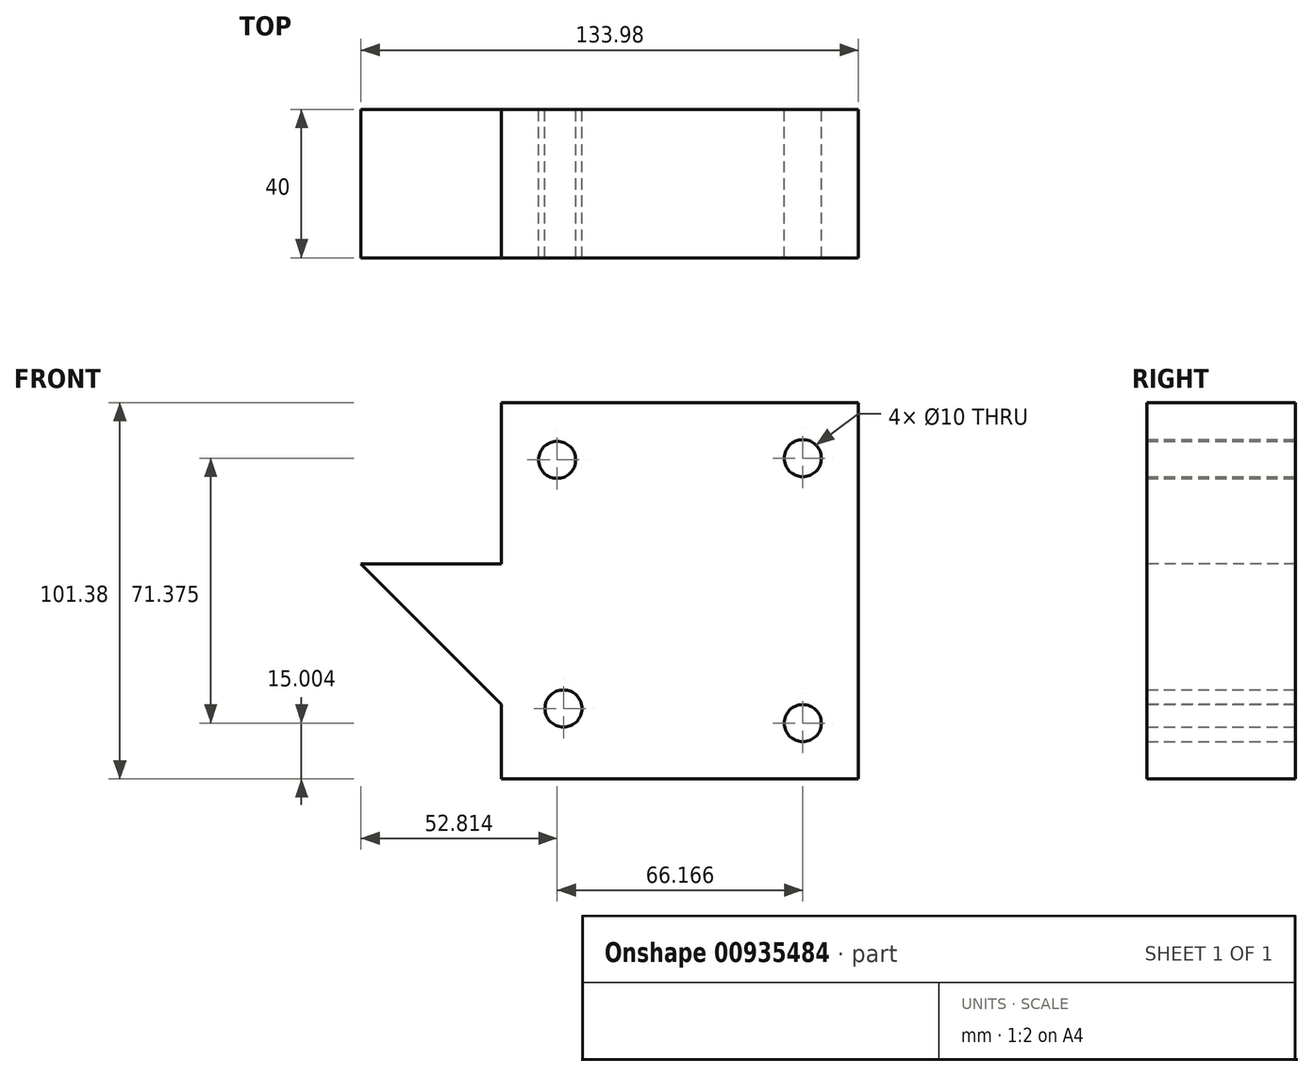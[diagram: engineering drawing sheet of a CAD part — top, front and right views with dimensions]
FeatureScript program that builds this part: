
annotation { "Feature Type Name" : "Feature", "Feature Type Description" : "" }
export const myFeature = defineFeature(function(context is Context, id is Id, definition is map)
    precondition{}
    {
        {
            var Q0;
            Q0=qCreatedBy(makeId("Front.planeOp"),FACE);
            var sketch = newSketch(context, id + "F0", { "sketchPlane" : qUnion([Q0])});
            skLineSegment(sketch, "E0", {"start": v(-1231.13, 861.68) * mm, "end": v(1231.13, 861.68) * mm});
            skLineSegment(sketch, "E1", {"start": v(1231.13, 861.68) * mm, "end": v(1231.13, -874.17) * mm});
            skLineSegment(sketch, "E2", {"start": v(1231.13, -874.17) * mm, "end": v(-1231.13, -874.17) * mm});
            skLineSegment(sketch, "E3", {"start": v(-1231.13, -874.17) * mm, "end": v(-1231.13, 861.68) * mm});
            skLineSegment(sketch, "E4", {"start": v(-731.13, 861.68) * mm, "end": v(-731.13, -874.17) * mm});
            skLineSegment(sketch, "E5.bottom", {"start": v(-55.5, 55.06) * mm, "end": v(40.67, 55.06) * mm});
            skLineSegment(sketch, "E5.top", {"start": v(-55.5, -46.32) * mm, "end": v(40.67, -46.32) * mm});
            skLineSegment(sketch, "E5.left", {"start": v(-55.5, 55.06) * mm, "end": v(-55.5, -46.32) * mm});
            skLineSegment(sketch, "E5.right", {"start": v(40.67, 55.06) * mm, "end": v(40.67, -46.32) * mm});
            skSolve(sketch);
        }
        {
            var Q0;
            Q0=makeQuery(id+"F0.imprint","IMPRINT",FACE,{"disambiguationData":[TD([[makeQuery(id+"F0.imprint","IMPRINT",EDGE,{"derivedFrom":sQuery(id+"F0.wireOp",EDGE,"E5.bottom")}),-1.0]])]});
            extrude(context, id + "F1", {"entities" : qUnion([Q0]), "depth" : 40 * mm, "offsetDistance" : 25 * mm});
        }
        {
            var Q0;
            Q0=makeQuery(id+"F1.opExtrude","CAP_FACE",FACE,{"disambiguationData":[OSD([sQuery(id+"F0.wireOp",EDGE,"E5.bottom"),sQuery(id+"F0.wireOp",EDGE,"E5.top"),sQuery(id+"F0.wireOp",EDGE,"E5.left"),sQuery(id+"F0.wireOp",EDGE,"E5.right")])],"isStart":false});
            var sketch = newSketch(context, id + "F2", { "sketchPlane" : qUnion([Q0])});
            skLineSegment(sketch, "E6", {"start": v(-55.5, -26.28) * mm, "end": v(-93.3, 11.53) * mm});
            skLineSegment(sketch, "E7", {"start": v(-93.3, 11.53) * mm, "end": v(-55.5, 11.53) * mm});
            skLineSegment(sketch, "E8", {"start": v(-55.5, 11.53) * mm, "end": v(-55.5, -26.28) * mm});
            skSolve(sketch);
        }
        {
            var Q0;
            Q0=makeQuery(id+"F2.imprint","IMPRINT",FACE,{"disambiguationData":[TD([[makeQuery(id+"F2.imprint","IMPRINT",EDGE,{"derivedFrom":sQuery(id+"F2.wireOp",EDGE,"E6")}),-1.0]])]});
            extrude(context, id + "F3", {"entities" : qUnion([Q0]), "operationType" : NewBodyOperationType.ADD, "oppositeDirection" : true, "depth" : 40 * mm, "offsetDistance" : 25 * mm});
        }
        {
            var Q0;
            Q0=makeQuery(id+"F3.boolean.opBoolean","MERGE",FACE,{"derivedFrom":[makeQuery(id+"F1.opExtrude","CAP_FACE",FACE,{"disambiguationData":[OSD([sQuery(id+"F0.wireOp",EDGE,"E5.bottom"),sQuery(id+"F0.wireOp",EDGE,"E5.top"),sQuery(id+"F0.wireOp",EDGE,"E5.left"),sQuery(id+"F0.wireOp",EDGE,"E5.right")])],"isStart":true}),makeQuery(id+"F3.opExtrude","CAP_FACE",FACE,{"disambiguationData":[OSD([sQuery(id+"F2.wireOp",EDGE,"E6"),sQuery(id+"F2.wireOp",EDGE,"E7"),sQuery(id+"F2.wireOp",EDGE,"E8")])],"isStart":false})]});
            var sketch = newSketch(context, id + "F4", { "sketchPlane" : qUnion([Q0])});
            skCircle(sketch, "E9", {"center": v(-25.67, -31.32) * mm, "radius": 5 * mm});
            skCircle(sketch, "E10", {"center": v(-25.67, 40.06) * mm, "radius": 5 * mm});
            skCircle(sketch, "E11", {"center": v(40.5, 39.62) * mm, "radius": 5 * mm});
            skCircle(sketch, "E12", {"center": v(38.79, -27.37) * mm, "radius": 5 * mm});
            skSolve(sketch);
        }
        {
            var Q0;
            Q0=makeQuery(id+"F4.imprint","IMPRINT",FACE,{"disambiguationData":[TD([[makeQuery(id+"F4.imprint","IMPRINT",EDGE,{"derivedFrom":sQuery(id+"F4.wireOp",EDGE,"E12")}),1.0]])]});
            var Q1;
            Q1=makeQuery(id+"F4.imprint","IMPRINT",FACE,{"disambiguationData":[TD([[makeQuery(id+"F4.imprint","IMPRINT",EDGE,{"derivedFrom":sQuery(id+"F4.wireOp",EDGE,"E9")}),1.0]])]});
            var Q2;
            Q2=makeQuery(id+"F4.imprint","IMPRINT",FACE,{"disambiguationData":[TD([[makeQuery(id+"F4.imprint","IMPRINT",EDGE,{"derivedFrom":sQuery(id+"F4.wireOp",EDGE,"E10")}),1.0]])]});
            var Q3;
            Q3=makeQuery(id+"F4.imprint","IMPRINT",FACE,{"disambiguationData":[TD([[makeQuery(id+"F4.imprint","IMPRINT",EDGE,{"derivedFrom":sQuery(id+"F4.wireOp",EDGE,"E11")}),1.0]])]});
            extrude(context, id + "F5", {"entities" : qUnion([Q0, Q1, Q2, Q3]), "operationType" : NewBodyOperationType.REMOVE, "endBound" : BoundingType.THROUGH_ALL, "oppositeDirection" : true, "depth" : 25 * mm, "offsetDistance" : 25 * mm});
        }
    });
